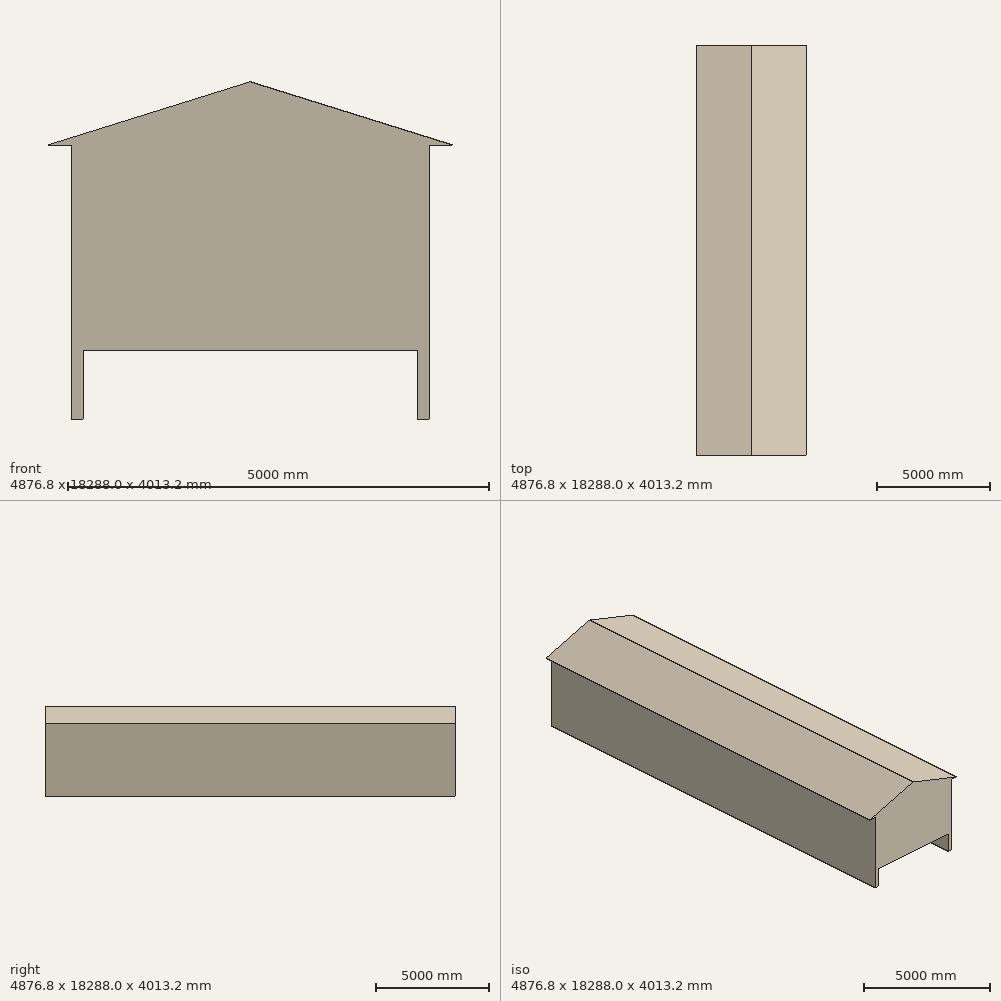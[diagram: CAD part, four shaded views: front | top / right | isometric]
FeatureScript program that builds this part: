
annotation { "Feature Type Name" : "Feature", "Feature Type Description" : "" }
export const myFeature = defineFeature(function(context is Context, id is Id, definition is map)
    precondition{}
    {
        {
            var Q0;
            Q0=qCreatedBy(makeId("Front.planeOp"),FACE);
            var sketch = newSketch(context, id + "F0", { "sketchPlane" : qUnion([Q0])});
            skLineSegment(sketch, "E0.top", {"start": v(1981.2, 812.8) * mm, "end": v(-1981.2, 812.8) * mm});
            skLineSegment(sketch, "E0.left", {"start": v(2133.6, 3251.2) * mm, "end": v(2133.6, 812.8) * mm});
            skLineSegment(sketch, "E0.right", {"start": v(-2133.6, 3251.2) * mm, "end": v(-2133.6, 812.8) * mm});
            skPoint(sketch, "E0.middle", {"position": v(0, 2032) * mm});
            skLineSegment(sketch, "E1", {"start": v(-2133.6, 3251.2) * mm, "end": v(-2438.4, 3251.2) * mm});
            skLineSegment(sketch, "E2", {"start": v(-2438.4, 3251.2) * mm, "end": v(0, 4013.2) * mm});
            skLineSegment(sketch, "E3", {"start": v(0, 4013.2) * mm, "end": v(2438.4, 3251.2) * mm});
            skLineSegment(sketch, "E4", {"start": v(2438.4, 3251.2) * mm, "end": v(2133.6, 3251.2) * mm});
            skLineSegment(sketch, "E5", {"start": v(-2133.6, 812.8) * mm, "end": v(-2133.6, 0) * mm});
            skLineSegment(sketch, "E6", {"start": v(-2133.6, 0) * mm, "end": v(-1981.2, 0) * mm});
            skLineSegment(sketch, "E7", {"start": v(-1981.2, 0) * mm, "end": v(-1981.2, 812.8) * mm});
            skLineSegment(sketch, "E8", {"start": v(2133.6, 812.8) * mm, "end": v(2133.6, 0) * mm});
            skLineSegment(sketch, "E9", {"start": v(2133.6, 0) * mm, "end": v(1981.2, 0) * mm});
            skLineSegment(sketch, "E10", {"start": v(1981.2, 0) * mm, "end": v(1981.2, 812.8) * mm});
            skSolve(sketch);
        }
        {
            var Q0;
            Q0=makeQuery(id+"F0.imprint","IMPRINT",FACE,{"disambiguationData":[TD([[makeQuery(id+"F0.imprint","IMPRINT",EDGE,{"derivedFrom":sQuery(id+"F0.wireOp",EDGE,"E0.top")}),-1.0]])]});
            extrude(context, id + "F1", {"entities" : qUnion([Q0]), "endBound" : BoundingType.SYMMETRIC, "depth" : 18288 * mm});
        }
    });
